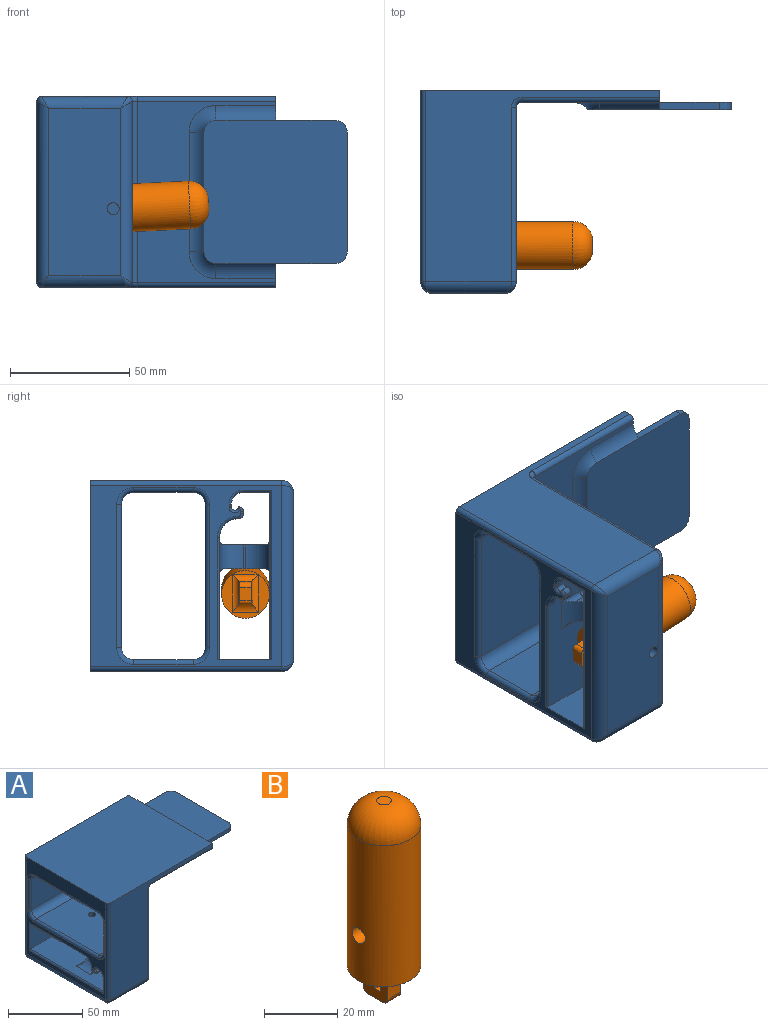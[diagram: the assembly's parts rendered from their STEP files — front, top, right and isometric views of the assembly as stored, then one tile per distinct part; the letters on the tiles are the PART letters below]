
ASSEMBLY  parts=2 mates=1
PART A: 115 faces, bbox 130.1x86.7x85.1 mm
  f0: plane 98x80mm, normal (0,-1,0), area 3069.4mm2, adj f8,f25,f27,f31,f35,f111,f112
  f1: cylinder r=2mm len=3.53mm, axis (-1,0,0), area 0.5mm2, adj f59,f65,f104,f105
  f2: plane 80x76mm, normal (-1,0,0), area 1692.8mm2, adj f8,f11,f23,f31,f33,f73,f74,f75
  f3: plane 3x1mm, normal (0,0,-1), area 3mm2, adj f58,f59,f100,f106
  f4: plane 39x25mm, normal (0,1,0), area 780.5mm2, adj f5,f10,f12,f44,f47,f56,f57,f95
  f5: plane 76x73mm, normal (1,0,0), area 954.1mm2, adj f4,f11,f26,f27,f29,f43,f48,f49
  f6: plane 76x58mm, normal (0,0,-1), area 1834.9mm2, adj f35,f43,f66,f67,f68,f69,f70,f111
  f7: plane 98x80mm, normal (0,1,0), area 3069.4mm2, adj f8,f24,f29,f33,f35,f113,f114
  f8: plane 100x80mm, normal (0,0,1), area 7998.3mm2, adj f0,f2,f7,f31,f33,f35
  f9: plane 70x30mm, normal (0,0,-1), area 2080.4mm2, adj f14,f23,f24,f25,f26
  f10: plane 70x37mm, normal (0,0,1), area 2367.2mm2, adj f4,f11,f14,f56,f71,f87,f88,f90
  f11: plane 40x25mm, normal (0,-1,0), area 842.1mm2, adj f2,f5,f10,f12,f56,f57,f93,f94
  f12: plane 70.05x37.05mm, normal (0,0,-1), area 2276.5mm2, adj f4,f11,f13,f46,f57,f72,f81,f82
  f13: cylinder r=2.5mm len=6mm, axis (0,0,-1), area 94.2mm2, adj f12,f15
  f14: cylinder r=2.5mm len=10mm, axis (0,0,-1), area 157.1mm2, adj f9,f10
  f15: plane 60x36mm, normal (0,0,1), area 2140.4mm2, adj f13,f19,f20,f49,f80
  f16: plane 60x36mm, normal (0,0,-1), area 2160mm2, adj f21,f22,f54,f73
  f17: plane 36x25mm, normal (0,-1,0), area 900mm2, adj f20,f21,f50,f76
  f18: plane 36x25mm, normal (0,1,0), area 900mm2, adj f19,f22,f53,f77
  f19: cylinder r=5mm len=36mm, axis (1,0,0), area 282.7mm2, adj f15,f18,f51,f79
  f20: cylinder r=5mm len=36mm, axis (-1,0,0), area 282.7mm2, adj f15,f17,f48,f78
  f21: cylinder r=5mm len=36mm, axis (1,0,0), area 282.7mm2, adj f16,f17,f52,f74
  f22: cylinder r=5mm len=36mm, axis (-1,0,0), area 282.7mm2, adj f16,f18,f55,f75
  f23: cylinder r=5mm len=76mm, axis (0,1,0), area 579.8mm2, adj f2,f9,f32,f34
  f24: cylinder r=5mm len=36mm, axis (1,0,0), area 265.6mm2, adj f7,f9,f30,f34
  f25: cylinder r=5mm len=36mm, axis (-1,0,0), area 265.6mm2, adj f0,f9,f28,f32
  f26: cylinder r=5mm len=76mm, axis (0,1,0), area 579.8mm2, adj f5,f9,f28,f30
  f27: cylinder r=2mm len=73mm, axis (0,0,1), area 229.3mm2, adj f0,f5,f28,f112
  f28: bspline ~5.91x5mm, area 16.7mm2, adj f25,f26,f27
  f29: cylinder r=2mm len=73mm, axis (0,0,-1), area 229.3mm2, adj f5,f7,f30,f114
  f30: bspline ~5.91x5mm, area 16.7mm2, adj f24,f26,f29
  f31: cylinder r=2mm len=80mm, axis (0,0,1), area 251.3mm2, adj f0,f2,f8,f32
  f32: bspline ~5.91x5mm, area 16.7mm2, adj f23,f25,f31
  f33: cylinder r=2mm len=80mm, axis (0,0,-1), area 251.3mm2, adj f2,f7,f8,f34
  f34: bspline ~5.23x5mm, area 16.7mm2, adj f23,f24,f33
  f35: plane 80x8mm, normal (1,0,0), area 409.7mm2, adj f0,f6,f7,f8,f36,f37,f38,f66
  f36: plane 60x30mm, normal (0,0,1), area 1789.3mm2, adj f35,f37,f38,f39,f41,f42
  f37: plane 25x3mm, normal (0,-1,0), area 75mm2, adj f35,f36,f40,f42
  f38: plane 25x3mm, normal (0,1,0), area 75mm2, adj f35,f36,f40,f41
  f39: plane 50x3mm, normal (1,0,0), area 150mm2, adj f36,f40,f41,f42
  f40: plane 60x60mm, normal (0,0,-1), area 3578.5mm2, adj f37,f38,f39,f41,f42,f66,f67,f68
  f41: cylinder r=5mm len=5mm, axis (0,0,-1), area 23.6mm2, adj f36,f38,f39,f40
  f42: cylinder r=5mm len=5mm, axis (0,0,1), area 23.6mm2, adj f36,f37,f39,f40
  f43: cylinder r=2mm len=76mm, axis (0,1,0), area 238.8mm2, adj f5,f6,f112,f114
  f44: plane 13.34x9mm, normal (1,0,0), area 63.3mm2, adj f4,f45,f47,f60,f65,f105,f106,f107
  f45: plane 4x1mm, normal (0,0,-1), area 4mm2, adj f44,f47,f60,f99
  f46: cylinder r=8mm len=8mm, axis (-1,0,0), area 37.7mm2, adj f12,f58,f96,f110
  f47: cylinder r=5mm len=5mm, axis (-1,0,0), area 31.4mm2, adj f4,f44,f45,f97
  f48: torus R=7mm, axis (-1,0,0), area 28.3mm2, adj f5,f20,f49,f50
  f49: cylinder r=2mm len=60mm, axis (0,-1,0), area 188.5mm2, adj f5,f15,f48,f51
  f50: cylinder r=2mm len=25mm, axis (0,0,-1), area 78.5mm2, adj f5,f17,f48,f52
  f51: torus R=7mm, axis (-1,0,0), area 28.3mm2, adj f5,f19,f49,f53
  f52: torus R=7mm, axis (-1,0,0), area 28.3mm2, adj f5,f21,f50,f54
  f53: cylinder r=2mm len=25mm, axis (0,0,1), area 78.5mm2, adj f5,f18,f51,f55
  f54: cylinder r=2mm len=60mm, axis (0,1,0), area 188.5mm2, adj f5,f16,f52,f55
  f55: torus R=7mm, axis (-1,0,0), area 28.3mm2, adj f5,f22,f53,f54
  f56: cylinder r=2mm len=70mm, axis (0,1,0), area 219.9mm2, adj f4,f5,f10,f11
  f57: cylinder r=2mm len=70mm, axis (0,-1,0), area 219.9mm2, adj f4,f5,f11,f12
  f58: cylinder r=2mm len=3mm, axis (1,0,0), area 9.4mm2, adj f3,f46,f98,f108
  f59: cylinder r=2mm len=3mm, axis (-1,0,0), area 9.4mm2, adj f1,f3,f102,f105
  f60: cylinder r=2mm len=4mm, axis (-1,0,0), area 0.6mm2, adj f44,f45,f65,f101
  f61: plane 17x6mm, normal (1,0,0), area 102mm2, adj f83,f86,f89,f92
  f62: plane 17x5mm, normal (0,-1,0), area 36.3mm2, adj f63,f71,f72,f82,f88,f89
  f63: plane 10x1mm, normal (-1,0,0), area 10mm2, adj f62,f64,f71,f72
  f64: plane 17x5mm, normal (0,1,0), area 36.3mm2, adj f63,f71,f72,f81,f86,f87
  f65: cylinder r=1.5mm len=4mm, axis (1,0,0), area 17.8mm2, adj f1,f44,f60,f103,f105
  f66: cylinder r=8mm len=25mm, axis (1,0,0), area 179.1mm2, adj f6,f35,f40,f67
  f67: torus R=11.24mm, axis (0,0,1), area 88.9mm2, adj f6,f40,f66,f68
  f68: cylinder r=8mm len=50mm, axis (0,1,0), area 358.3mm2, adj f6,f40,f67,f69
  f69: torus R=11.24mm, axis (0,0,1), area 88.9mm2, adj f6,f40,f68,f70
  f70: cylinder r=8mm len=25mm, axis (1,0,0), area 179.1mm2, adj f6,f35,f40,f69
  f71: cylinder r=10mm len=14mm, axis (0,1,0), area 167mm2, adj f10,f62,f63,f64,f87,f88
  f72: cylinder r=10mm len=14mm, axis (0,1,0), area 167mm2, adj f12,f62,f63,f64,f81,f82
  f73: cylinder r=2mm len=60mm, axis (0,-1,0), area 188.5mm2, adj f2,f16,f74,f75
  f74: torus R=7mm, axis (-1,0,0), area 28.3mm2, adj f2,f21,f73,f76
  f75: torus R=7mm, axis (-1,0,0), area 28.3mm2, adj f2,f22,f73,f77
  f76: cylinder r=2mm len=25mm, axis (0,0,1), area 78.5mm2, adj f2,f17,f74,f78
  f77: cylinder r=2mm len=25mm, axis (0,0,-1), area 78.5mm2, adj f2,f18,f75,f79
  f78: torus R=7mm, axis (-1,0,0), area 28.3mm2, adj f2,f20,f76,f80
  f79: torus R=7mm, axis (-1,0,0), area 28.3mm2, adj f2,f19,f77,f80
  f80: cylinder r=2mm len=60mm, axis (0,1,0), area 188.5mm2, adj f2,f15,f78,f79
  f81: cylinder r=2mm len=11mm, axis (1,0,0), area 24.4mm2, adj f12,f64,f72,f84
  f82: cylinder r=2mm len=11mm, axis (-1,0,0), area 24.4mm2, adj f12,f62,f72,f85
  f83: cylinder r=2mm len=6mm, axis (0,-1,0), area 18.8mm2, adj f12,f61,f84,f85
  f84: torus R=4mm, axis (0,0,-1), area 13.5mm2, adj f12,f81,f83,f86
  f85: torus R=4mm, axis (0,0,-1), area 13.5mm2, adj f12,f82,f83,f89
  f86: cylinder r=2mm len=17mm, axis (0,0,1), area 53.4mm2, adj f61,f64,f84,f90
  f87: cylinder r=2mm len=11mm, axis (1,0,0), area 24.4mm2, adj f10,f64,f71,f90
  f88: cylinder r=2mm len=11mm, axis (-1,0,0), area 24.4mm2, adj f10,f62,f71,f91
  f89: cylinder r=2mm len=17mm, axis (0,0,-1), area 53.4mm2, adj f61,f62,f85,f91
  f90: torus R=4mm, axis (0,0,-1), area 13.5mm2, adj f10,f86,f87,f92
  f91: torus R=4mm, axis (0,0,-1), area 13.5mm2, adj f10,f88,f89,f92
  f92: cylinder r=2mm len=6mm, axis (0,-1,0), area 18.8mm2, adj f10,f61,f90,f91
  f93: cylinder r=1mm len=71mm, axis (0,1,0), area 110.5mm2, adj f2,f10,f11,f95
  f94: cylinder r=1mm len=51mm, axis (0,-1,0), area 80.1mm2, adj f2,f11,f12,f96
  f95: cylinder r=1mm len=12mm, axis (0,0,-1), area 17.8mm2, adj f2,f4,f93,f97
  f96: torus R=9mm, axis (-1,0,0), area 20.6mm2, adj f2,f46,f94,f98
  f97: torus R=6mm, axis (-1,0,0), area 13.2mm2, adj f2,f47,f95,f99
  f98: torus R=1mm, axis (-1,0,0), area 4mm2, adj f2,f58,f96,f100
  f99: cylinder r=1mm len=1mm, axis (0,-1,0), area 1.6mm2, adj f2,f45,f97,f101
  f100: cylinder r=1mm len=1mm, axis (0,-1,0), area 1.6mm2, adj f2,f3,f98,f102
  f101: torus R=3mm, axis (-1,0,0), area 0.3mm2, adj f2,f60,f99,f103
  f102: torus R=1mm, axis (-1,0,0), area 3.5mm2, adj f2,f59,f100,f103,f104
  f103: torus R=2.5mm, axis (-1,0,0), area 8.3mm2, adj f2,f65,f101,f102,f104
  f104: torus R=3mm, axis (-1,0,0), area 0mm2, adj f1,f102,f103
  f105: torus R=1mm, axis (-1,0,0), area 4.2mm2, adj f1,f44,f59,f65,f106
  f106: cylinder r=1mm len=1mm, axis (0,1,0), area 1.6mm2, adj f3,f44,f105,f108
  f107: cylinder r=1mm len=13.34mm, axis (0,-1,0), area 21mm2, adj f4,f12,f44,f109
  f108: torus R=1mm, axis (-1,0,0), area 4mm2, adj f44,f58,f106,f110
  f109: bspline ~5.79x2mm, area 4.4mm2, adj f12,f107,f110
  f110: torus R=9mm, axis (-1,0,0), area 15.6mm2, adj f44,f46,f108,f109
  f111: cylinder r=2mm len=58mm, axis (1,0,0), area 182.2mm2, adj f0,f6,f35,f112
  f112: torus R=4mm, axis (0,1,0), area 13.5mm2, adj f0,f27,f43,f111
  f113: cylinder r=2mm len=58mm, axis (-1,0,0), area 182.2mm2, adj f6,f7,f35,f114
  f114: torus R=4mm, axis (0,1,0), area 13.5mm2, adj f7,f29,f43,f113
PART B: 23 faces, bbox 20.1x20.1x65.1 mm
  f0: plane 10.54x1.5mm, normal (0,0,-1), area 10.7mm2, adj f3,f19
  f1: plane 5.53x5mm, normal (0,-1,0), area 27.6mm2, adj f6,f7,f15,f20
  f2: plane 20x18.35mm, normal (0,0,-1), area 127mm2, adj f3,f17,f18,f22
  f3: cylinder r=10mm len=47mm, axis (0,0,-1), area 2913.5mm2, adj f0,f2,f5,f9,f17,f18,f19
  f4: plane 4x4mm, normal (0,0,1), area 12.6mm2, adj f5
  f5: torus R=2mm, axis (0,0,1), area 560mm2, adj f3,f4
  f6: plane 9.5x7.53mm, normal (1,0,0), area 57.6mm2, adj f1,f8,f10,f12,f13,f14,f15,f17
  f7: plane 9.5x7.53mm, normal (-1,0,0), area 57.6mm2, adj f1,f8,f10,f12,f13,f14,f15,f18
  f8: plane 5.5x5mm, normal (0,0,-1), area 27.5mm2, adj f6,f7,f20,f21
  f9: cylinder r=2.5mm len=20mm, axis (1,0,0), area 309.2mm2, adj f3
  f10: plane 5x5mm, normal (0,1,0), area 25mm2, adj f6,f7,f19,f21
  f11: plane 5.34x2mm, normal (0,0,-1), area 10.7mm2, adj f12,f16,f17,f18
  f12: plane 5.34x5mm, normal (0,-1,0), area 25.1mm2, adj f6,f7,f11,f13,f17,f18
  f13: plane 5x2mm, normal (0,0,1), area 10mm2, adj f6,f7,f12,f14
  f14: plane 5x4mm, normal (0,1,0), area 20mm2, adj f6,f7,f13,f15
  f15: plane 5x3mm, normal (0,0.17,0.98), area 15.2mm2, adj f1,f6,f7,f14
  f16: plane 5.91x3.07mm, normal (0,-0.17,-0.98), area 17mm2, adj f11,f17,f18,f22
  f17: cylinder r=3mm len=15.95mm, axis (0,1,0), area 49.1mm2, adj f2,f3,f6,f11,f12,f16,f19,f22
  f18: cylinder r=3mm len=15.95mm, axis (0,-1,0), area 49.1mm2, adj f2,f3,f7,f11,f12,f16,f19,f22
  f19: cylinder r=3mm len=10.82mm, axis (-1,0,0), area 33.8mm2, adj f0,f3,f10,f17,f18
  f20: cylinder r=2mm len=5mm, axis (1,0,0), area 15.7mm2, adj f1,f6,f7,f8
  f21: cylinder r=2mm len=5mm, axis (-1,0,0), area 15.7mm2, adj f6,f7,f8,f10
  f22: cylinder r=5mm len=11mm, axis (1,0,0), area 32.2mm2, adj f2,f16,f17,f18
PLACE A rot(axis=(-1,0,0),90deg) t=(70.64,107.97,-5.94)mm fixed
PLACE B rot(axis=(0.57,0.57,0.6),118.4deg) t=(87.66,48.1,-53.67)mm
MATE revolute B.f9 <-> A.f13  axis (0,1,0) through (102.64,37.97,-52.94)mm
